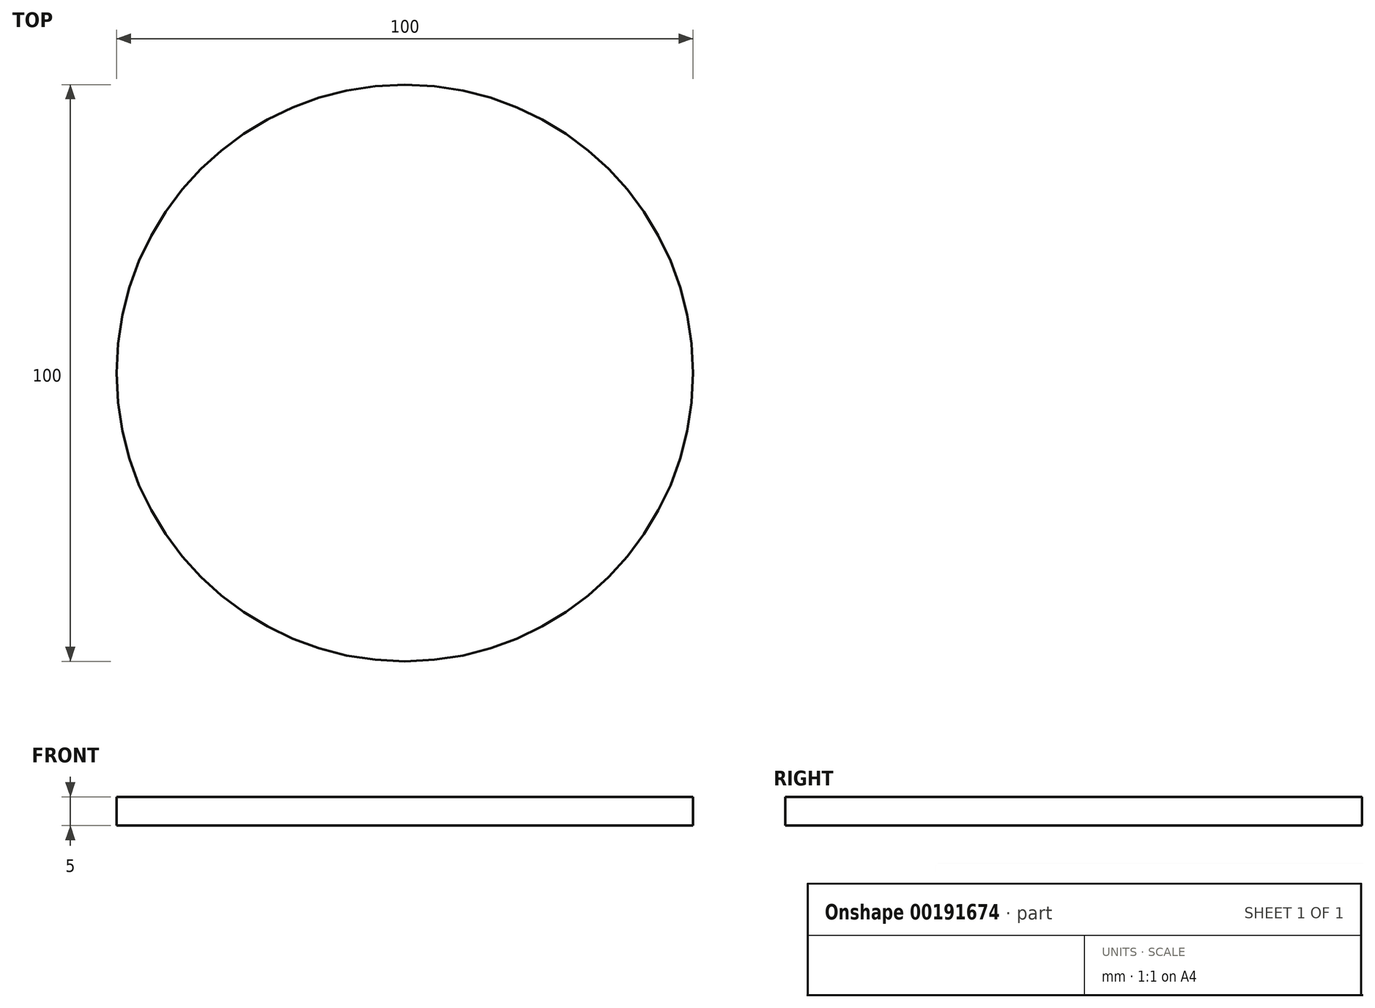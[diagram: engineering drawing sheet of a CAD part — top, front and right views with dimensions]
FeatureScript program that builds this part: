
annotation { "Feature Type Name" : "Feature", "Feature Type Description" : "" }
export const myFeature = defineFeature(function(context is Context, id is Id, definition is map)
    precondition{}
    {
        {
            var Q0;
            Q0=qCreatedBy(makeId("Top.planeOp"),FACE);
            var sketch = newSketch(context, id + "F0", { "sketchPlane" : qUnion([Q0])});
            skCircle(sketch, "E0", {"center": v(0, 0) * mm, "radius": 50 * mm});
            skSolve(sketch);
        }
        {
            var Q0;
            Q0 = qSketchRegion(id + "F0", true);
            extrude(context, id + "F1", {"entities" : qUnion([Q0]), "depth" : 5 * mm});
        }
    });
